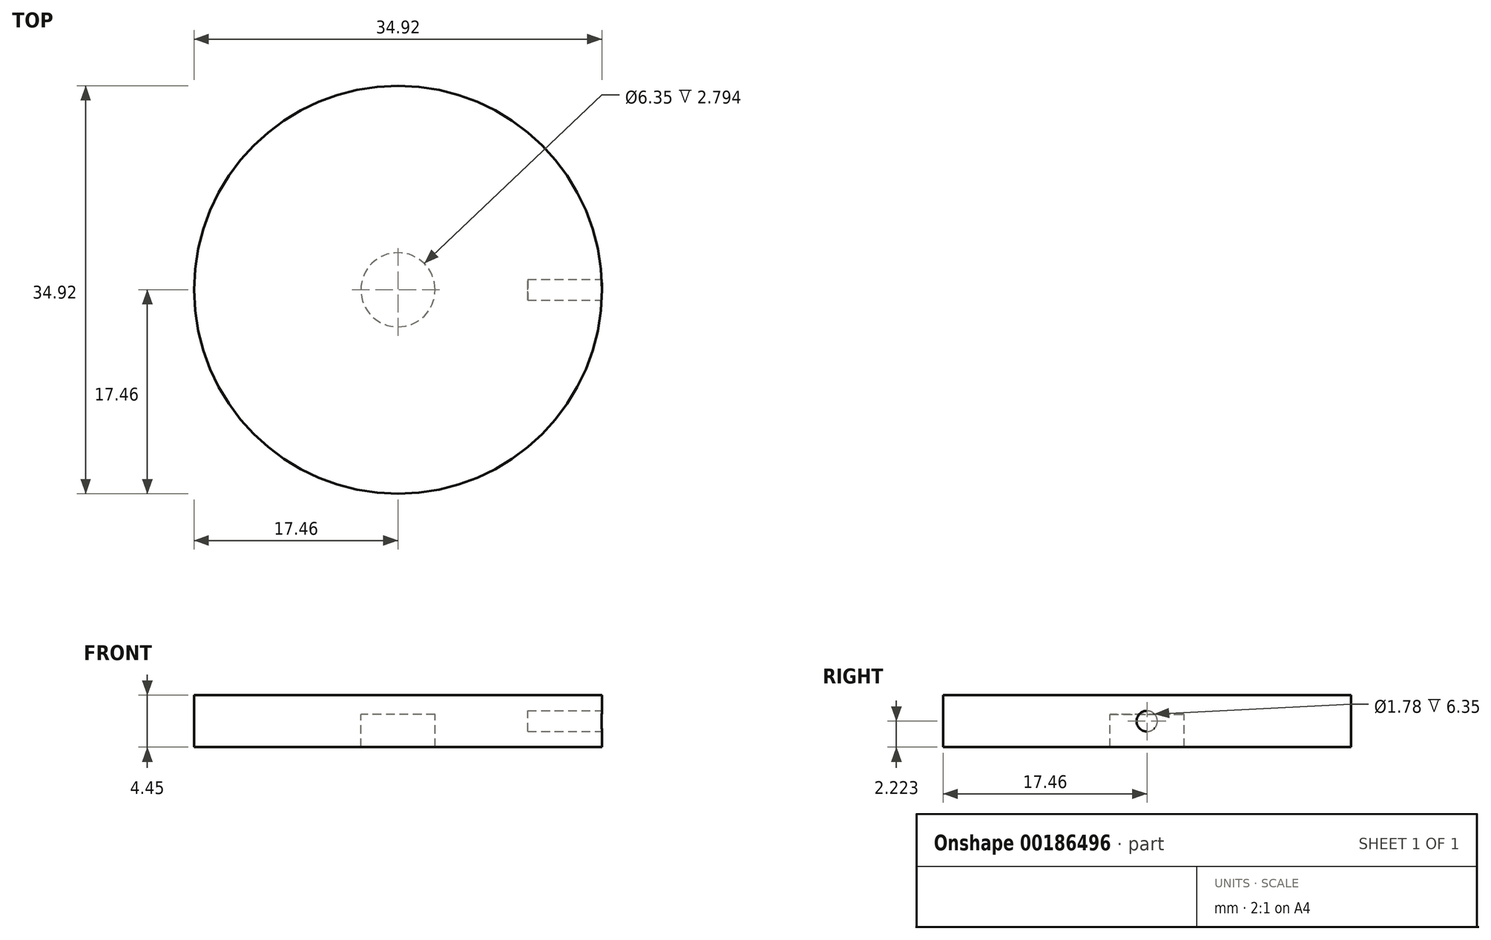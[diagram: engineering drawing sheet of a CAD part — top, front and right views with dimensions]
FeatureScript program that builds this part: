
annotation { "Feature Type Name" : "Feature", "Feature Type Description" : "" }
export const myFeature = defineFeature(function(context is Context, id is Id, definition is map)
    precondition{}
    {
        {
            var Q0;
            Q0=qCreatedBy(makeId("Right.planeOp"),FACE);
            var sketch = newSketch(context, id + "F0", { "sketchPlane" : qUnion([Q0])});
            skLineSegment(sketch, "E0", {"start": v(-3.18, 2.54) * mm, "end": v(-17.46, 2.54) * mm});
            skLineSegment(sketch, "E1", {"start": v(-17.46, 2.54) * mm, "end": v(-17.46, 6.99) * mm});
            skLineSegment(sketch, "E2", {"start": v(-17.46, 6.99) * mm, "end": v(0, 6.99) * mm});
            skLineSegment(sketch, "E3", {"start": v(0, 6.99) * mm, "end": v(0, 5.33) * mm});
            skLineSegment(sketch, "E4", {"start": v(0, 5.33) * mm, "end": v(-3.18, 5.33) * mm});
            skLineSegment(sketch, "E5", {"start": v(-3.18, 5.33) * mm, "end": v(-3.18, 2.54) * mm});
            skSolve(sketch);
        }
        {
            var Q0;
            Q0 = qSketchRegion(id + "F0", true);
            var Q1;
            Q1=sQuery(id+"F0.wireOp",EDGE,"E3");
            revolve(context, id + "F1", {"entities" : qUnion([Q0]), "axis" : qUnion([Q1]), "revolveType" : RevolveType.FULL});
        }
        {
            var Q0;
            Q0=qCreatedBy(makeId("Right.planeOp"),FACE);
            cPlane(context, id + "F2", {"entities" : qUnion([Q0]), "cplaneType" : CPlaneType.OFFSET, "offset" : 17.46 * mm, "width" : 152.4 * mm, "height" : 152.4 * mm});
        }
        {
            var Q0;
            Q0=qCreatedBy(id+"F2.planeOp",FACE);
            var sketch = newSketch(context, id + "F3", { "sketchPlane" : qUnion([Q0])});
            skCircle(sketch, "E6", {"center": v(0, 4.76) * mm, "radius": 0.89 * mm});
            skLineSegment(sketch, "E7", {"start": v(0, 6.99) * mm, "end": v(0, 2.54) * mm, "construction": true});
            skSolve(sketch);
        }
        {
            var Q0;
            Q0 = qSketchRegion(id + "F3", true);
            extrude(context, id + "F4", {"entities" : qUnion([Q0]), "operationType" : NewBodyOperationType.REMOVE, "oppositeDirection" : true, "depth" : 6.35 * mm});
        }
    });
